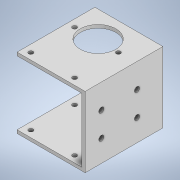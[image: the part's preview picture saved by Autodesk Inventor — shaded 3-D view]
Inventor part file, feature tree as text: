
AUTODESK INVENTOR PART (.ipt)
format: ipt  version: 2022 (Build 260153000, 153)  size: 164,352 bytes
history: native  units: mm
features: sketch x6, hole x4, extrude x2, other x1
ambient origin geometry x8: Origin, YZ Plane, XZ Plane, XY Plane, X Axis, Y Axis, Z Axis, Center Point
bodies: Body1 (feature_tree)
feature tree (13):
  other  "ソリッド1"
  extrude  "押し出し1"  Depth=48.0mm
  extrude  "押し出し2"  Depth=42.0mm
  hole  "穴1"  [1 undecoded]
  hole  "穴2"  [1 undecoded]
  hole  "穴3"  [1 undecoded]
  hole  "穴4"  [1 undecoded]
  sketch  "スケッチ1"
  sketch  "スケッチ2"
  sketch  "スケッチ3"
  sketch  "スケッチ4"
  sketch  "スケッチ5"
  sketch  "スケッチ6"
note: 4 required parameter values undecoded (feature->parameter linkage not recoverable at this tier; creation-order binding heuristic only, values carry confidence <= 0.55)
